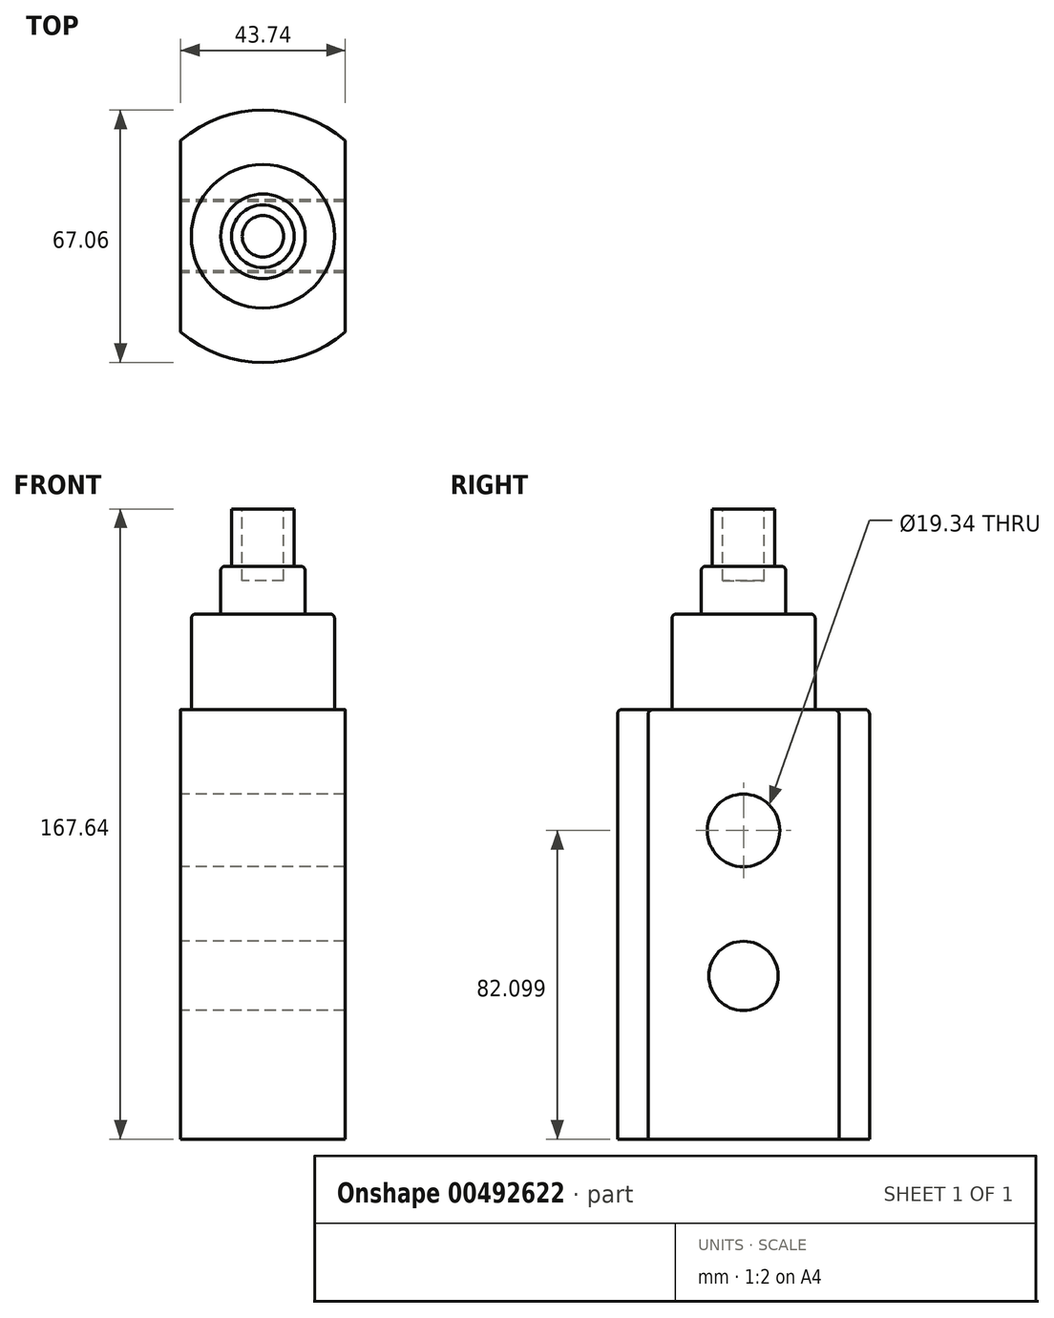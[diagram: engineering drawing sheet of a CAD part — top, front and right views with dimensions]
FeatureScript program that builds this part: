
annotation { "Feature Type Name" : "Feature", "Feature Type Description" : "" }
export const myFeature = defineFeature(function(context is Context, id is Id, definition is map)
    precondition{}
    {
        {
            var Q0;
            Q0=qCreatedBy(makeId("Top.planeOp"),FACE);
            var sketch = newSketch(context, id + "F0", { "sketchPlane" : qUnion([Q0])});
            skCircle(sketch, "E0", {"center": v(0, 0) * mm, "radius": 33.53 * mm});
            skSolve(sketch);
        }
        {
            var Q0;
            Q0 = qSketchRegion(id + "F0", true);
            extrude(context, id + "F1", {"entities" : qUnion([Q0]), "depth" : 114.3 * mm});
        }
        {
            var Q0;
            Q0=makeQuery(id+"F1.opExtrude","CAP_FACE",FACE,{"disambiguationData":[OSD([sQuery(id+"F0.wireOp",EDGE,"E0")])],"isStart":false});
            var sketch = newSketch(context, id + "F2", { "sketchPlane" : qUnion([Q0])});
            skCircle(sketch, "E1", {"center": v(0, 0) * mm, "radius": 19.06 * mm});
            skSolve(sketch);
        }
        {
            var Q0;
            Q0 = qSketchRegion(id + "F2", true);
            extrude(context, id + "F3", {"entities" : qUnion([Q0]), "operationType" : NewBodyOperationType.ADD, "depth" : 25.4 * mm});
        }
        {
            var Q0;
            Q0=makeQuery(id+"F3.opExtrude","CAP_FACE",FACE,{"disambiguationData":[OSD([sQuery(id+"F2.wireOp",EDGE,"E1")])],"isStart":false});
            var sketch = newSketch(context, id + "F4", { "sketchPlane" : qUnion([Q0])});
            skCircle(sketch, "E2", {"center": v(0, 0) * mm, "radius": 11.26 * mm});
            skSolve(sketch);
        }
        {
            var Q0;
            Q0=makeQuery(id+"F4.imprint","IMPRINT",FACE,{"disambiguationData":[TD([[makeQuery(id+"F4.imprint","IMPRINT",EDGE,{"derivedFrom":sQuery(id+"F4.wireOp",EDGE,"E2")}),1.0]])]});
            extrude(context, id + "F5", {"entities" : qUnion([Q0]), "operationType" : NewBodyOperationType.ADD, "depth" : 12.7 * mm});
        }
        {
            var Q0;
            Q0=makeQuery(id+"F5.opExtrude","CAP_FACE",FACE,{"disambiguationData":[OSD([sQuery(id+"F4.wireOp",EDGE,"E2")])],"isStart":false});
            var sketch = newSketch(context, id + "F6", { "sketchPlane" : qUnion([Q0])});
            skCircle(sketch, "E3", {"center": v(0, 0) * mm, "radius": 8.35 * mm});
            skSolve(sketch);
        }
        {
            var Q0;
            Q0 = qSketchRegion(id + "F6", true);
            extrude(context, id + "F7", {"entities" : qUnion([Q0]), "operationType" : NewBodyOperationType.ADD, "depth" : 2.54 * mm});
        }
        {
            var Q0;
            Q0=makeQuery(id+"F7.opExtrude","CAP_FACE",FACE,{"disambiguationData":[OSD([sQuery(id+"F6.wireOp",EDGE,"E3")])],"isStart":false});
            var sketch = newSketch(context, id + "F8", { "sketchPlane" : qUnion([Q0])});
            skCircle(sketch, "E4", {"center": v(0, 0) * mm, "radius": 8.35 * mm});
            skSolve(sketch);
        }
        {
            var Q0;
            Q0 = qSketchRegion(id + "F8", true);
            extrude(context, id + "F9", {"entities" : qUnion([Q0]), "operationType" : NewBodyOperationType.ADD, "depth" : 12.7 * mm});
        }
        {
            var Q0;
            Q0=makeQuery(id+"F9.opExtrude","CAP_FACE",FACE,{"disambiguationData":[OSD([sQuery(id+"F8.wireOp",EDGE,"E4")])],"isStart":false});
            var sketch = newSketch(context, id + "F10", { "sketchPlane" : qUnion([Q0])});
            skCircle(sketch, "E5", {"center": v(0, 0) * mm, "radius": 5.5 * mm});
            skSolve(sketch);
        }
        {
            var Q0;
            Q0=makeQuery(id+"F1.opExtrude","CAP_FACE",FACE,{"disambiguationData":[OSD([sQuery(id+"F0.wireOp",EDGE,"E0")])],"isStart":false});
            var sketch = newSketch(context, id + "F11", { "sketchPlane" : qUnion([Q0])});
            skLineSegment(sketch, "E6.bottom", {"start": v(21.87, 37.13) * mm, "end": v(39.14, 37.13) * mm});
            skLineSegment(sketch, "E6.top", {"start": v(21.87, -40.3) * mm, "end": v(39.14, -40.3) * mm});
            skLineSegment(sketch, "E6.left", {"start": v(21.87, 37.13) * mm, "end": v(21.87, -40.3) * mm});
            skLineSegment(sketch, "E6.right", {"start": v(39.14, 37.13) * mm, "end": v(39.14, -40.3) * mm});
            skSolve(sketch);
        }
        {
            var Q0;
            {var subQ4=sQuery(id+"F11.wireOp",EDGE,"E6.bottom");Q0=makeQuery(id+"F11.imprint","IMPRINT",FACE,{"disambiguationData":[TD([[makeQuery(id+"F11.imprint","IMPRINT",EDGE,{"derivedFrom":subQ4}),-1.0]])]});}
            var Q1;
            {var subQ0=sQuery(id+"F11.wireOp",EDGE,"E6.left");var subQ1=makeQuery(id+"F1.opExtrude","CAP_EDGE",EDGE,{"disambiguationData":[OSD([sQuery(id+"F0.wireOp",EDGE,"E0")])],"isStart":false});var subQ2=makeQuery(id+"F11.imprint","INTERSECT",VERTEX,{"disambiguationData":[OD(0.0)],"derivedFrom":[subQ1,subQ0]});Q1=makeQuery(id+"F11.imprint","IMPRINT",FACE,{"disambiguationData":[TD([[makeQuery(id+"F11.imprint","IMPRINT",EDGE,{"disambiguationData":[TD([[subQ2,-1.0]])],"derivedFrom":subQ0}),1.0]])]});}
            extrude(context, id + "F12", {"entities" : qUnion([Q0, Q1]), "operationType" : NewBodyOperationType.REMOVE, "oppositeDirection" : true, "depth" : 114.3 * mm});
        }
        {
            var Q0;
            Q0=makeQuery(id+"F1.opExtrude","CAP_FACE",FACE,{"disambiguationData":[OSD([sQuery(id+"F0.wireOp",EDGE,"E0")])],"isStart":false});
            var sketch = newSketch(context, id + "F13", { "sketchPlane" : qUnion([Q0])});
            skLineSegment(sketch, "E7.bottom", {"start": v(-21.87, 25.41) * mm, "end": v(-43.75, 25.41) * mm});
            skLineSegment(sketch, "E7.top", {"start": v(-21.87, -40.3) * mm, "end": v(-43.75, -40.3) * mm});
            skLineSegment(sketch, "E7.left", {"start": v(-21.87, 25.41) * mm, "end": v(-21.87, -40.3) * mm});
            skLineSegment(sketch, "E7.right", {"start": v(-43.75, 25.41) * mm, "end": v(-43.75, -40.3) * mm});
            skSolve(sketch);
        }
        {
            var Q0;
            Q0 = qSketchRegion(id + "F13", true);
            extrude(context, id + "F14", {"entities" : qUnion([Q0]), "operationType" : NewBodyOperationType.REMOVE, "oppositeDirection" : true, "depth" : 114.3 * mm});
        }
        {
            var Q0;
            Q0=makeQuery(id+"F14.boolean.opBoolean","COPY",FACE,{"derivedFrom":makeQuery(id+"F14.opExtrude","SWEPT_FACE",FACE,{"disambiguationData":[OSD([sQuery(id+"F13.wireOp",EDGE,"E7.left")])]})});
            var sketch = newSketch(context, id + "F15", { "sketchPlane" : qUnion([Q0])});
            skCircle(sketch, "E8", {"center": v(0, 82.1) * mm, "radius": 9.67 * mm});
            skCircle(sketch, "E9", {"center": v(0, 43.42) * mm, "radius": 9.2 * mm});
            skSolve(sketch);
        }
        {
            var Q0;
            Q0 = qSketchRegion(id + "F15", true);
            extrude(context, id + "F16", {"entities" : qUnion([Q0]), "operationType" : NewBodyOperationType.REMOVE, "oppositeDirection" : true, "depth" : 101.6 * mm});
        }
        {
            var Q0;
            Q0=makeQuery(id+"F3.opExtrude","CAP_EDGE",EDGE,{"disambiguationData":[OSD([sQuery(id+"F2.wireOp",EDGE,"E1")])],"isStart":false});
            fillet(context, id + "F17", {"entities" : qUnion([Q0]), "radius" : 1.27 * mm, "tangentPropagation" : true, "allowEdgeOverflow" : false});
        }
        {
            var Q0;
            Q0=makeQuery(id+"F5.opExtrude","CAP_EDGE",EDGE,{"disambiguationData":[OSD([sQuery(id+"F4.wireOp",EDGE,"E2")])],"isStart":false});
            fillet(context, id + "F18", {"entities" : qUnion([Q0]), "radius" : 1.27 * mm, "tangentPropagation" : true, "allowEdgeOverflow" : false});
        }
        {
            var Q0;
            Q0=makeQuery(id+"F14.boolean.opBoolean","SPLIT",EDGE,{"disambiguationData":[OD(0.0)],"derivedFrom":makeQuery(id+"F1.opExtrude","CAP_EDGE",EDGE,{"disambiguationData":[OSD([sQuery(id+"F0.wireOp",EDGE,"E0")])],"isStart":false})});
            var Q1;
            Q1=makeQuery(id+"F14.boolean.opBoolean","SPLIT",EDGE,{"disambiguationData":[OD(1.0)],"derivedFrom":makeQuery(id+"F1.opExtrude","CAP_EDGE",EDGE,{"disambiguationData":[OSD([sQuery(id+"F0.wireOp",EDGE,"E0")])],"isStart":false})});
            fillet(context, id + "F19", {"entities" : qUnion([Q0, Q1]), "radius" : 1.27 * mm, "tangentPropagation" : true, "allowEdgeOverflow" : false});
        }
        {
            var Q0;
            Q0 = qSketchRegion(id + "F10", true);
            extrude(context, id + "F20", {"entities" : qUnion([Q0]), "operationType" : NewBodyOperationType.REMOVE, "oppositeDirection" : true, "depth" : 19.05 * mm});
        }
    });
